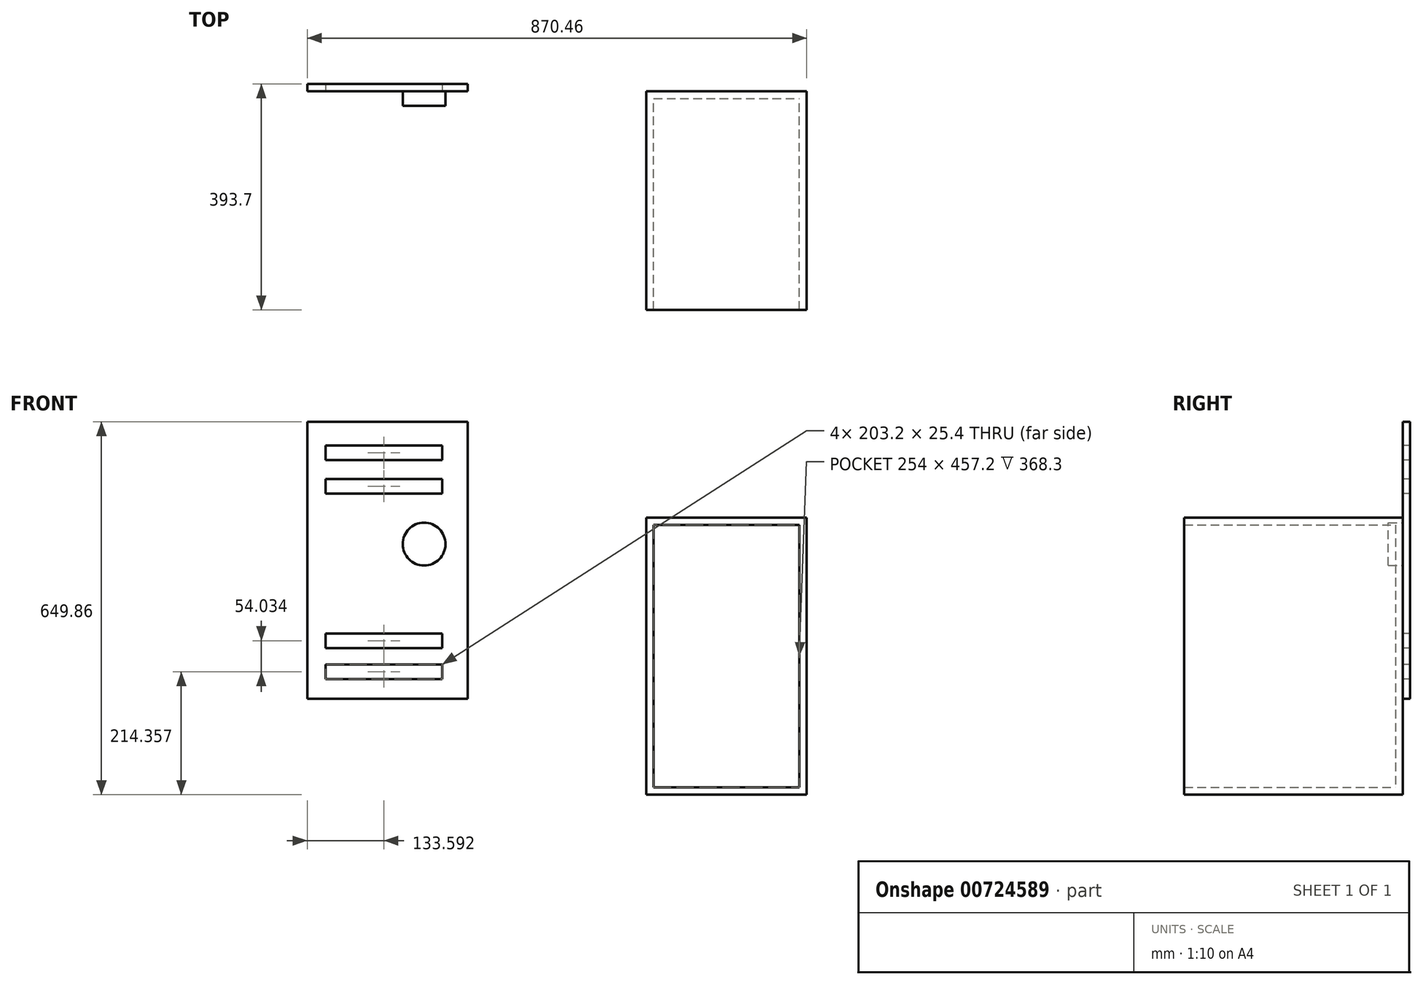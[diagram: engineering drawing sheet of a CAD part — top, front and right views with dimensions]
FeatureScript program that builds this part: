
annotation { "Feature Type Name" : "Feature", "Feature Type Description" : "" }
export const myFeature = defineFeature(function(context is Context, id is Id, definition is map)
    precondition{}
    {
        {
            var Q0;
            Q0=qCreatedBy(makeId("Front.planeOp"),FACE);
            var sketch = newSketch(context, id + "F0", { "sketchPlane" : qUnion([Q0])});
            skLineSegment(sketch, "E0.bottom", {"start": v(-150.57, 411.96) * mm, "end": v(128.83, 411.96) * mm});
            skLineSegment(sketch, "E0.top", {"start": v(-150.57, -70.64) * mm, "end": v(128.83, -70.64) * mm});
            skLineSegment(sketch, "E0.left", {"start": v(-150.57, 411.96) * mm, "end": v(-150.57, -70.64) * mm});
            skLineSegment(sketch, "E0.right", {"start": v(128.83, 411.96) * mm, "end": v(128.83, -70.64) * mm});
            skSolve(sketch);
        }
        {
            var Q0;
            Q0=makeQuery(id+"F0.imprint","IMPRINT",FACE,{"disambiguationData":[TD([[makeQuery(id+"F0.imprint","IMPRINT",EDGE,{"derivedFrom":sQuery(id+"F0.wireOp",EDGE,"E0.bottom")}),-1.0]])]});
            extrude(context, id + "F1", {"entities" : qUnion([Q0]), "depth" : 381 * mm, "offsetDistance" : 25.4 * mm});
        }
        {
            var Q0;
            Q0=makeQuery(id+"F1.opExtrude","CAP_FACE",FACE,{"disambiguationData":[OSD([sQuery(id+"F0.wireOp",EDGE,"E0.bottom"),sQuery(id+"F0.wireOp",EDGE,"E0.top"),sQuery(id+"F0.wireOp",EDGE,"E0.left"),sQuery(id+"F0.wireOp",EDGE,"E0.right")])],"isStart":true});
            var sketch = newSketch(context, id + "F2", { "sketchPlane" : qUnion([Q0])});
            skLineSegment(sketch, "E1.bottom", {"start": v(741.63, 579.22) * mm, "end": v(462.23, 579.22) * mm});
            skLineSegment(sketch, "E1.top", {"start": v(741.63, 96.62) * mm, "end": v(462.23, 96.62) * mm});
            skLineSegment(sketch, "E1.left", {"start": v(741.63, 579.22) * mm, "end": v(741.63, 96.62) * mm});
            skLineSegment(sketch, "E1.right", {"start": v(462.23, 579.22) * mm, "end": v(462.23, 96.62) * mm});
            skSolve(sketch);
        }
        {
            var Q0;
            Q0 = qSketchRegion(id + "F2", true);
            extrude(context, id + "F3", {"entities" : qUnion([Q0]), "depth" : 12.7 * mm, "offsetDistance" : 25.4 * mm});
        }
        {
            var Q0;
            Q0=makeQuery(id+"F1.opExtrude","CAP_FACE",FACE,{"disambiguationData":[OSD([sQuery(id+"F0.wireOp",EDGE,"E0.bottom"),sQuery(id+"F0.wireOp",EDGE,"E0.top"),sQuery(id+"F0.wireOp",EDGE,"E0.left"),sQuery(id+"F0.wireOp",EDGE,"E0.right")])],"isStart":false});
            shell(context, id + "F4", {"entities" : qUnion([Q0]), "thickness" : 12.7 * mm});
        }
        {
            var Q0;
            Q0=makeQuery(id+"F3.opExtrude","CAP_FACE",FACE,{"disambiguationData":[OSD([sQuery(id+"F2.wireOp",EDGE,"E1.bottom"),sQuery(id+"F2.wireOp",EDGE,"E1.top"),sQuery(id+"F2.wireOp",EDGE,"E1.left"),sQuery(id+"F2.wireOp",EDGE,"E1.right")])],"isStart":true});
            var sketch = newSketch(context, id + "F5", { "sketchPlane" : qUnion([Q0])});
            skLineSegment(sketch, "E2.bottom", {"start": v(-709.64, 537.87) * mm, "end": v(-506.44, 537.87) * mm});
            skLineSegment(sketch, "E2.top", {"start": v(-709.64, 512.47) * mm, "end": v(-506.44, 512.47) * mm});
            skLineSegment(sketch, "E2.left", {"start": v(-709.64, 537.87) * mm, "end": v(-709.64, 512.47) * mm});
            skLineSegment(sketch, "E2.right", {"start": v(-506.44, 537.87) * mm, "end": v(-506.44, 512.47) * mm});
            skLineSegment(sketch, "E3.bottom", {"start": v(-709.64, 131.02) * mm, "end": v(-506.44, 131.02) * mm});
            skLineSegment(sketch, "E3.top", {"start": v(-709.64, 156.42) * mm, "end": v(-506.44, 156.42) * mm});
            skLineSegment(sketch, "E3.left", {"start": v(-709.64, 131.02) * mm, "end": v(-709.64, 156.42) * mm});
            skLineSegment(sketch, "E3.right", {"start": v(-506.44, 131.02) * mm, "end": v(-506.44, 156.42) * mm});
            skLineSegment(sketch, "E4.bottom", {"start": v(-709.64, 185.05) * mm, "end": v(-506.44, 185.05) * mm});
            skLineSegment(sketch, "E4.top", {"start": v(-709.64, 210.45) * mm, "end": v(-506.44, 210.45) * mm});
            skLineSegment(sketch, "E4.left", {"start": v(-709.64, 185.05) * mm, "end": v(-709.64, 210.45) * mm});
            skLineSegment(sketch, "E4.right", {"start": v(-506.44, 185.05) * mm, "end": v(-506.44, 210.45) * mm});
            skLineSegment(sketch, "E5.bottom", {"start": v(-709.64, 479.8) * mm, "end": v(-506.44, 479.8) * mm});
            skLineSegment(sketch, "E5.top", {"start": v(-709.64, 454.4) * mm, "end": v(-506.44, 454.4) * mm});
            skLineSegment(sketch, "E5.left", {"start": v(-709.64, 479.8) * mm, "end": v(-709.64, 454.4) * mm});
            skLineSegment(sketch, "E5.right", {"start": v(-506.44, 479.8) * mm, "end": v(-506.44, 454.4) * mm});
            skSolve(sketch);
        }
        {
            var Q0;
            Q0=makeQuery(id+"F5.imprint","IMPRINT",FACE,{"disambiguationData":[TD([[makeQuery(id+"F5.imprint","IMPRINT",EDGE,{"derivedFrom":sQuery(id+"F5.wireOp",EDGE,"E2.bottom")}),-1.0]])]});
            var Q1;
            Q1=makeQuery(id+"F5.imprint","IMPRINT",FACE,{"disambiguationData":[TD([[makeQuery(id+"F5.imprint","IMPRINT",EDGE,{"derivedFrom":sQuery(id+"F5.wireOp",EDGE,"E5.bottom")}),-1.0]])]});
            var Q2;
            Q2=makeQuery(id+"F5.imprint","IMPRINT",FACE,{"disambiguationData":[TD([[makeQuery(id+"F5.imprint","IMPRINT",EDGE,{"derivedFrom":sQuery(id+"F5.wireOp",EDGE,"E4.bottom")}),1.0]])]});
            var Q3;
            Q3=makeQuery(id+"F5.imprint","IMPRINT",FACE,{"disambiguationData":[TD([[makeQuery(id+"F5.imprint","IMPRINT",EDGE,{"derivedFrom":sQuery(id+"F5.wireOp",EDGE,"E3.bottom")}),1.0]])]});
            extrude(context, id + "F6", {"entities" : qUnion([Q0, Q1, Q2, Q3]), "operationType" : NewBodyOperationType.REMOVE, "oppositeDirection" : true, "depth" : 25.4 * mm, "offsetDistance" : 25.4 * mm});
        }
        {
            var Q0;
            Q0=makeQuery(id+"F3.opExtrude","CAP_FACE",FACE,{"disambiguationData":[OSD([sQuery(id+"F2.wireOp",EDGE,"E1.bottom"),sQuery(id+"F2.wireOp",EDGE,"E1.top"),sQuery(id+"F2.wireOp",EDGE,"E1.left"),sQuery(id+"F2.wireOp",EDGE,"E1.right")])],"isStart":true});
            var sketch = newSketch(context, id + "F7", { "sketchPlane" : qUnion([Q0])});
            skCircle(sketch, "E6", {"center": v(-537.94, 366.11) * mm, "radius": 37.35 * mm});
            skSolve(sketch);
        }
        {
            var Q0;
            Q0 = qSketchRegion(id + "F7", true);
            extrude(context, id + "F8", {"entities" : qUnion([Q0]), "operationType" : NewBodyOperationType.ADD, "depth" : 25.4 * mm, "offsetDistance" : 25.4 * mm});
        }
    });
